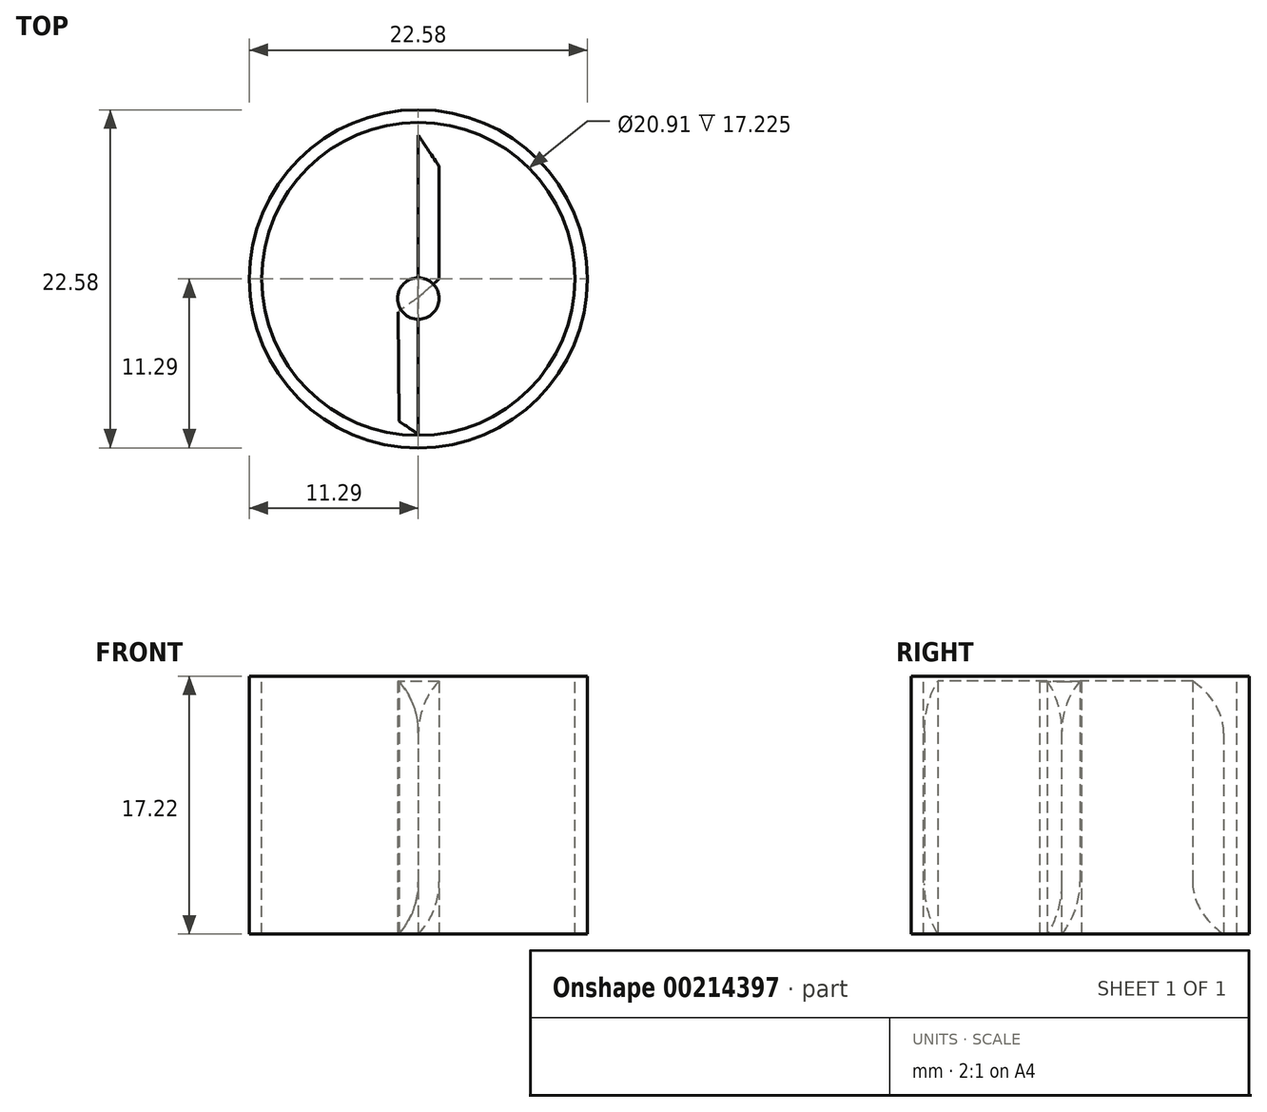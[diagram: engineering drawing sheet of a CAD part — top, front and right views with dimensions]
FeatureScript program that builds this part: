
annotation { "Feature Type Name" : "Feature", "Feature Type Description" : "" }
export const myFeature = defineFeature(function(context is Context, id is Id, definition is map)
    precondition{}
    {
        {
            var Q0;
            Q0=qCreatedBy(makeId("Top.planeOp"),FACE);
            var sketch = newSketch(context, id + "F0", { "sketchPlane" : qUnion([Q0])});
            skCircle(sketch, "E0", {"center": v(0, 0) * mm, "radius": 11.3 * mm});
            skSolve(sketch);
        }
        {
            var Q0;
            Q0 = qSketchRegion(id + "F0", true);
            extrude(context, id + "F1", {"entities" : qUnion([Q0]), "depth" : 17.22 * mm});
        }
        {
            var Q0;
            Q0=makeQuery(id+"F1.opExtrude","CAP_FACE",FACE,{"disambiguationData":[OSD([sQuery(id+"F0.wireOp",EDGE,"E0")])],"isStart":false});
            var sketch = newSketch(context, id + "F2", { "sketchPlane" : qUnion([Q0])});
            skCircle(sketch, "E1", {"center": v(0, 0) * mm, "radius": 10.45 * mm});
            skSolve(sketch);
        }
        {
            var Q0;
            Q0 = qSketchRegion(id + "F2", true);
            extrude(context, id + "F3", {"entities" : qUnion([Q0]), "operationType" : NewBodyOperationType.REMOVE, "oppositeDirection" : true, "depth" : 25.4 * mm});
        }
        {
            var Q0;
            Q0=qCreatedBy(makeId("Top.planeOp"),FACE);
            var sketch = newSketch(context, id + "F10", { "sketchPlane" : qUnion([Q0])});
            skLineSegment(sketch, "E2", {"start": v(0, 0) * mm, "end": v(0, 9.59) * mm});
            skLineSegment(sketch, "E3", {"start": v(0, 9.59) * mm, "end": v(1.4, 7.51) * mm});
            skLineSegment(sketch, "E4", {"start": v(1.4, 7.51) * mm, "end": v(1.4, 0) * mm});
            skLineSegment(sketch, "E5", {"start": v(1.4, 0) * mm, "end": v(0, -1.24) * mm});
            skLineSegment(sketch, "E6", {"start": v(0, -1.24) * mm, "end": v(0, -1.24) * mm});
            skLineSegment(sketch, "E7", {"start": v(0, -1.24) * mm, "end": v(-1.36, -2.21) * mm});
            skLineSegment(sketch, "E8", {"start": v(-1.36, -2.21) * mm, "end": v(-1.29, -9.5) * mm});
            skLineSegment(sketch, "E9", {"start": v(-1.29, -9.5) * mm, "end": v(0, -10.38) * mm});
            skLineSegment(sketch, "E10", {"start": v(0, -10.38) * mm, "end": v(0, 0) * mm});
            skSolve(sketch);
        }
        {
            var Q0;
            Q0 = qSketchRegion(id + "F10", true);
            extrude(context, id + "F4", {"entities" : qUnion([Q0]), "depth" : 16.92 * mm});
        }
        {
            var Q0;
            Q0=qCreatedBy(makeId("Top.planeOp"),FACE);
            var sketch = newSketch(context, id + "F5", { "sketchPlane" : qUnion([Q0])});
            skCircle(sketch, "E11", {"center": v(0, -1.3) * mm, "radius": 1.39 * mm});
            skSolve(sketch);
        }
        {
            var Q0;
            Q0 = qSketchRegion(id + "F5", true);
            extrude(context, id + "F6", {"entities" : qUnion([Q0]), "depth" : 16.86 * mm});
        }
        {
            var Q0;
            Q0=makeQuery(id+"F4.opExtrude","CAP_EDGE",EDGE,{"disambiguationData":[OSD([sQuery(id+"F10.wireOp",EDGE,"E4")])],"isStart":true});
            fillet(context, id + "F7", {"entities" : qUnion([Q0]), "radius" : 5.08 * mm, "tangentPropagation" : true, "allowEdgeOverflow" : false});
        }
        {
            var Q0;
            Q0=makeQuery(id+"F4.opExtrude","CAP_EDGE",EDGE,{"disambiguationData":[OSD([sQuery(id+"F10.wireOp",EDGE,"E2"),sQuery(id+"F10.wireOp",EDGE,"E10")])],"isStart":false});
            fillet(context, id + "F8", {"entities" : qUnion([Q0]), "radius" : 5.08 * mm, "tangentPropagation" : true, "allowEdgeOverflow" : false});
        }
        {
            var Q0;
            Q0=makeQuery(id+"F4.opExtrude","CAP_EDGE",EDGE,{"disambiguationData":[OSD([sQuery(id+"F10.wireOp",EDGE,"E10")])],"isStart":false});
            fillet(context, id + "F9", {"entities" : qUnion([Q0]), "radius" : 5.08 * mm, "tangentPropagation" : true, "allowEdgeOverflow" : false});
        }
        {
            var Q0;
            Q0=makeQuery(id+"F4.opExtrude","CAP_EDGE",EDGE,{"disambiguationData":[OSD([sQuery(id+"F10.wireOp",EDGE,"E10")])],"isStart":true});
            fillet(context, id + "F11", {"entities" : qUnion([Q0]), "radius" : 5.08 * mm, "tangentPropagation" : true, "allowEdgeOverflow" : false});
        }
    });
